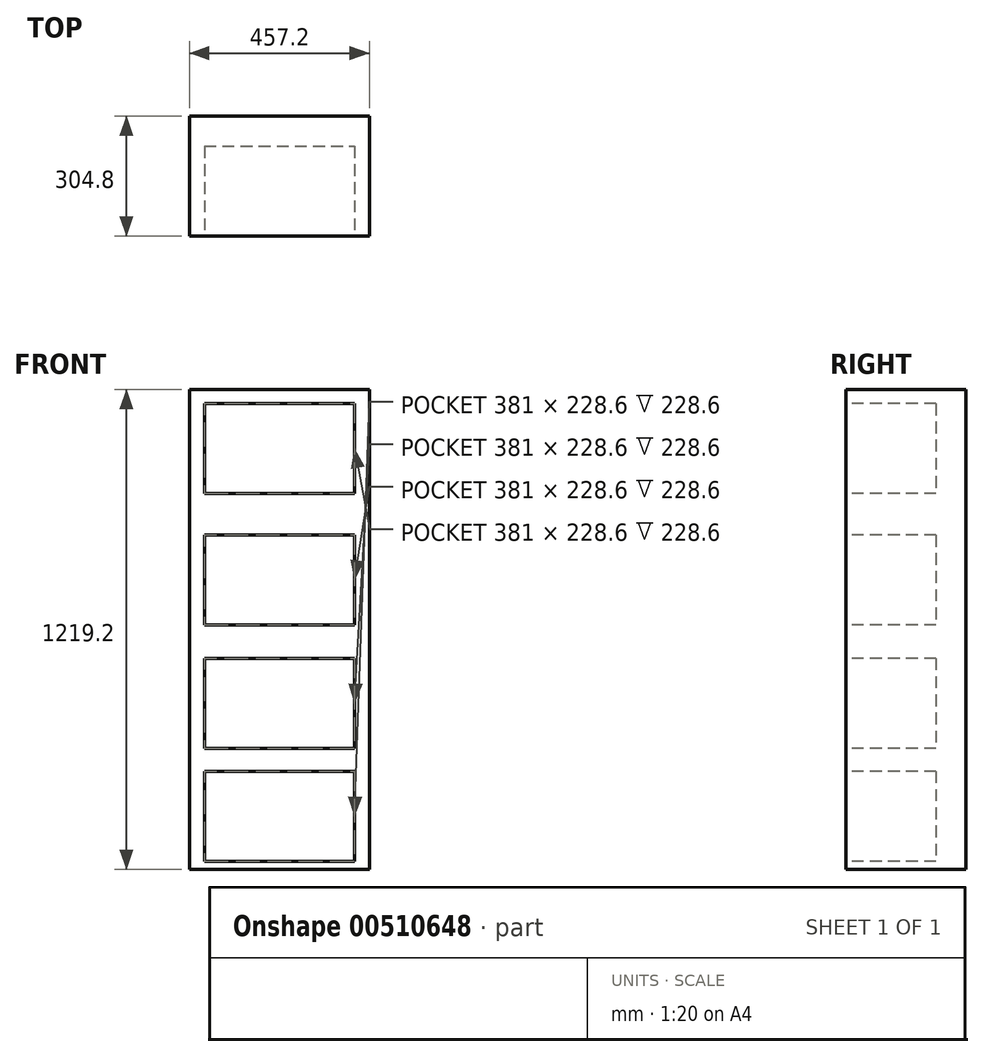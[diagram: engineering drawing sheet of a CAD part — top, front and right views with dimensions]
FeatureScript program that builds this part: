
annotation { "Feature Type Name" : "Feature", "Feature Type Description" : "" }
export const myFeature = defineFeature(function(context is Context, id is Id, definition is map)
    precondition{}
    {
        {
            var Q0;
            Q0=qCreatedBy(makeId("Top.planeOp"),FACE);
            var sketch = newSketch(context, id + "F0", { "sketchPlane" : qUnion([Q0])});
            skLineSegment(sketch, "E0", {"start": v(-254.5, 177.55) * mm, "end": v(-254.5, -127.25) * mm});
            skLineSegment(sketch, "E1", {"start": v(-254.5, -127.25) * mm, "end": v(202.7, -127.25) * mm});
            skLineSegment(sketch, "E2", {"start": v(202.7, -127.25) * mm, "end": v(202.7, 177.55) * mm});
            skLineSegment(sketch, "E3", {"start": v(202.7, 177.55) * mm, "end": v(-254.5, 177.55) * mm});
            skSolve(sketch);
        }
        {
            var Q0;
            Q0 = qSketchRegion(id + "F0", true);
            extrude(context, id + "F1", {"entities" : qUnion([Q0]), "depth" : 1219.2 * mm, "offsetDistance" : 30.48 * mm});
        }
        {
            var Q0;
            Q0=makeQuery(id+"F1.opExtrude","SWEPT_FACE",FACE,{"disambiguationData":[OSD([sQuery(id+"F0.wireOp",EDGE,"E1")])]});
            var sketch = newSketch(context, id + "F2", { "sketchPlane" : qUnion([Q0])});
            skLineSegment(sketch, "E4.bottom", {"start": v(-216.4, 1183.7) * mm, "end": v(164.6, 1183.7) * mm});
            skLineSegment(sketch, "E4.top", {"start": v(-216.4, 955.1) * mm, "end": v(164.6, 955.1) * mm});
            skLineSegment(sketch, "E4.left", {"start": v(-216.4, 1183.7) * mm, "end": v(-216.4, 955.1) * mm});
            skLineSegment(sketch, "E4.right", {"start": v(164.6, 1183.7) * mm, "end": v(164.6, 955.1) * mm});
            skLineSegment(sketch, "E5.bottom", {"start": v(-216.4, 849.68) * mm, "end": v(164.6, 849.68) * mm});
            skLineSegment(sketch, "E5.top", {"start": v(-216.4, 621.08) * mm, "end": v(164.6, 621.08) * mm});
            skLineSegment(sketch, "E5.left", {"start": v(-216.4, 849.68) * mm, "end": v(-216.4, 621.08) * mm});
            skLineSegment(sketch, "E5.right", {"start": v(164.6, 849.68) * mm, "end": v(164.6, 621.08) * mm});
            skLineSegment(sketch, "E6.bottom", {"start": v(-216.4, 536.53) * mm, "end": v(164.6, 536.53) * mm});
            skLineSegment(sketch, "E6.top", {"start": v(-216.4, 307.93) * mm, "end": v(164.6, 307.93) * mm});
            skLineSegment(sketch, "E6.left", {"start": v(-216.4, 536.53) * mm, "end": v(-216.4, 307.93) * mm});
            skLineSegment(sketch, "E6.right", {"start": v(164.6, 536.53) * mm, "end": v(164.6, 307.93) * mm});
            skLineSegment(sketch, "E7.bottom", {"start": v(-216.4, 249.48) * mm, "end": v(164.6, 249.48) * mm});
            skLineSegment(sketch, "E7.top", {"start": v(-216.4, 20.88) * mm, "end": v(164.6, 20.88) * mm});
            skLineSegment(sketch, "E7.left", {"start": v(-216.4, 249.48) * mm, "end": v(-216.4, 20.88) * mm});
            skLineSegment(sketch, "E7.right", {"start": v(164.6, 249.48) * mm, "end": v(164.6, 20.88) * mm});
            skSolve(sketch);
        }
        {
            var Q0;
            Q0 = qSketchRegion(id + "F2", true);
            extrude(context, id + "F3", {"entities" : qUnion([Q0]), "operationType" : NewBodyOperationType.REMOVE, "oppositeDirection" : true, "depth" : 228.6 * mm, "offsetDistance" : 30.48 * mm});
        }
    });
